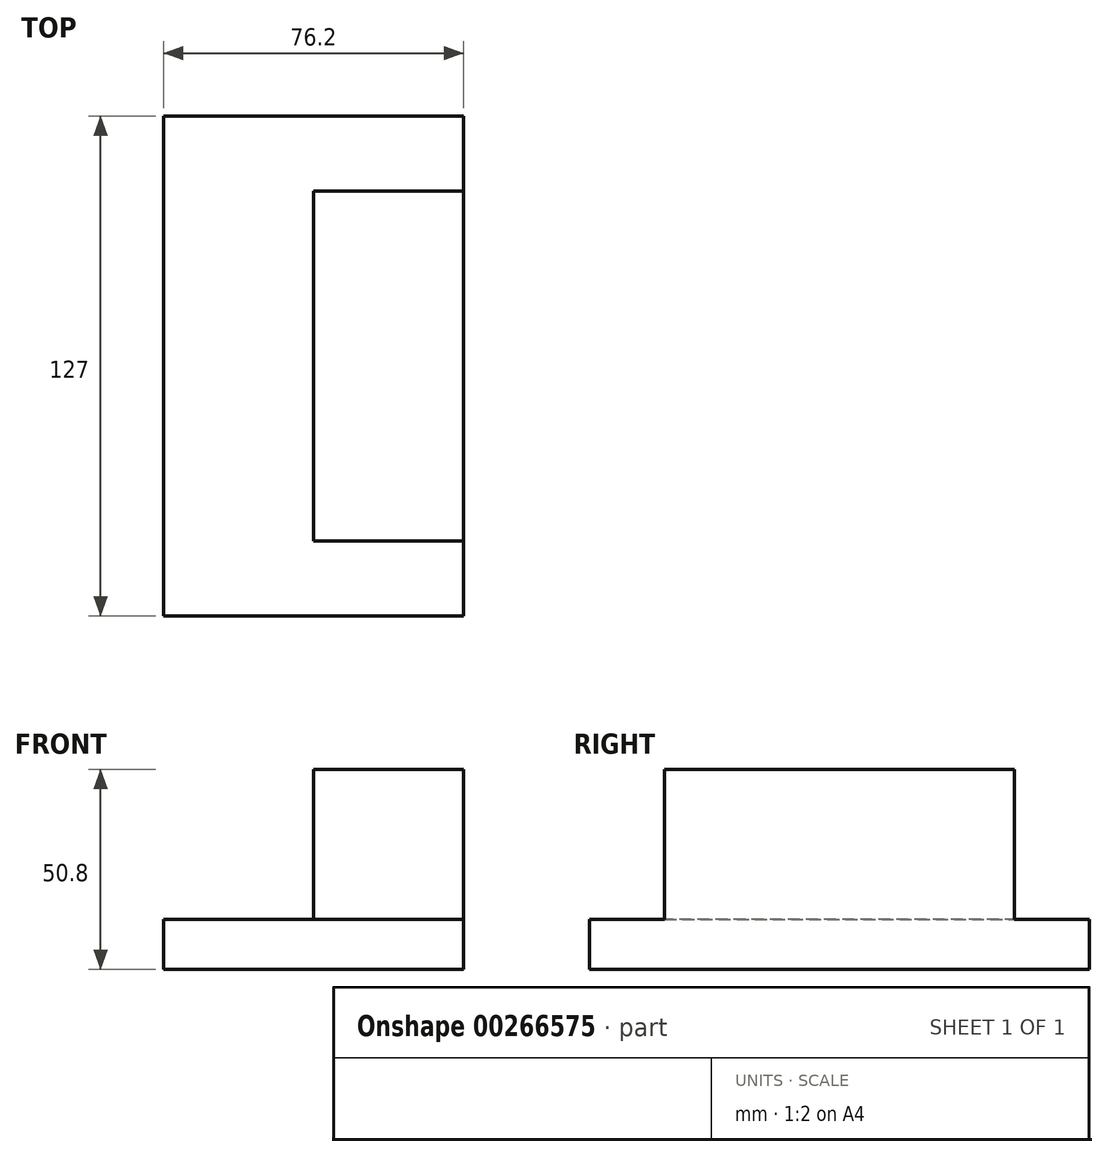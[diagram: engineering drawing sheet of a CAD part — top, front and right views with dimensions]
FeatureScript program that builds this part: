
annotation { "Feature Type Name" : "Feature", "Feature Type Description" : "" }
export const myFeature = defineFeature(function(context is Context, id is Id, definition is map)
    precondition{}
    {
        {
            var Q0;
            Q0=qCreatedBy(makeId("Top.planeOp"),FACE);
            var sketch = newSketch(context, id + "F0", { "sketchPlane" : qUnion([Q0])});
            skLineSegment(sketch, "E0.bottom", {"start": v(-38.1, 63.5) * mm, "end": v(38.1, 63.5) * mm});
            skLineSegment(sketch, "E0.top", {"start": v(-38.1, -63.5) * mm, "end": v(38.1, -63.5) * mm});
            skLineSegment(sketch, "E0.left", {"start": v(-38.1, 63.5) * mm, "end": v(-38.1, -63.5) * mm});
            skLineSegment(sketch, "E0.right", {"start": v(38.1, 63.5) * mm, "end": v(38.1, -63.5) * mm});
            skPoint(sketch, "E0.middle", {"position": v(0, 0) * mm});
            skSolve(sketch);
        }
        {
            var Q0;
            Q0=makeQuery(id+"F0.imprint","IMPRINT",FACE,{"disambiguationData":[TD([[makeQuery(id+"F0.imprint","IMPRINT",EDGE,{"derivedFrom":sQuery(id+"F0.wireOp",EDGE,"E0.bottom")}),-1.0]])]});
            extrude(context, id + "F1", {"entities" : qUnion([Q0]), "depth" : 12.7 * mm});
        }
        {
            var Q0;
            Q0=qCreatedBy(makeId("Right.planeOp"),FACE);
            var sketch = newSketch(context, id + "F2", { "sketchPlane" : qUnion([Q0])});
            skLineSegment(sketch, "E1.bottom", {"start": v(-44.45, 50.8) * mm, "end": v(44.45, 50.8) * mm});
            skLineSegment(sketch, "E1.top", {"start": v(-44.45, 12.7) * mm, "end": v(44.45, 12.7) * mm});
            skLineSegment(sketch, "E1.left", {"start": v(-44.45, 50.8) * mm, "end": v(-44.45, 12.7) * mm});
            skLineSegment(sketch, "E1.right", {"start": v(44.45, 50.8) * mm, "end": v(44.45, 12.7) * mm});
            skSolve(sketch);
        }
        {
            var Q0;
            Q0=makeQuery(id+"F2.imprint","IMPRINT",FACE,{"disambiguationData":[TD([[makeQuery(id+"F2.imprint","IMPRINT",EDGE,{"derivedFrom":sQuery(id+"F2.wireOp",EDGE,"E1.bottom")}),-1.0]])]});
            extrude(context, id + "F3", {"entities" : qUnion([Q0]), "operationType" : NewBodyOperationType.ADD, "depth" : 38.1 * mm});
        }
    });
